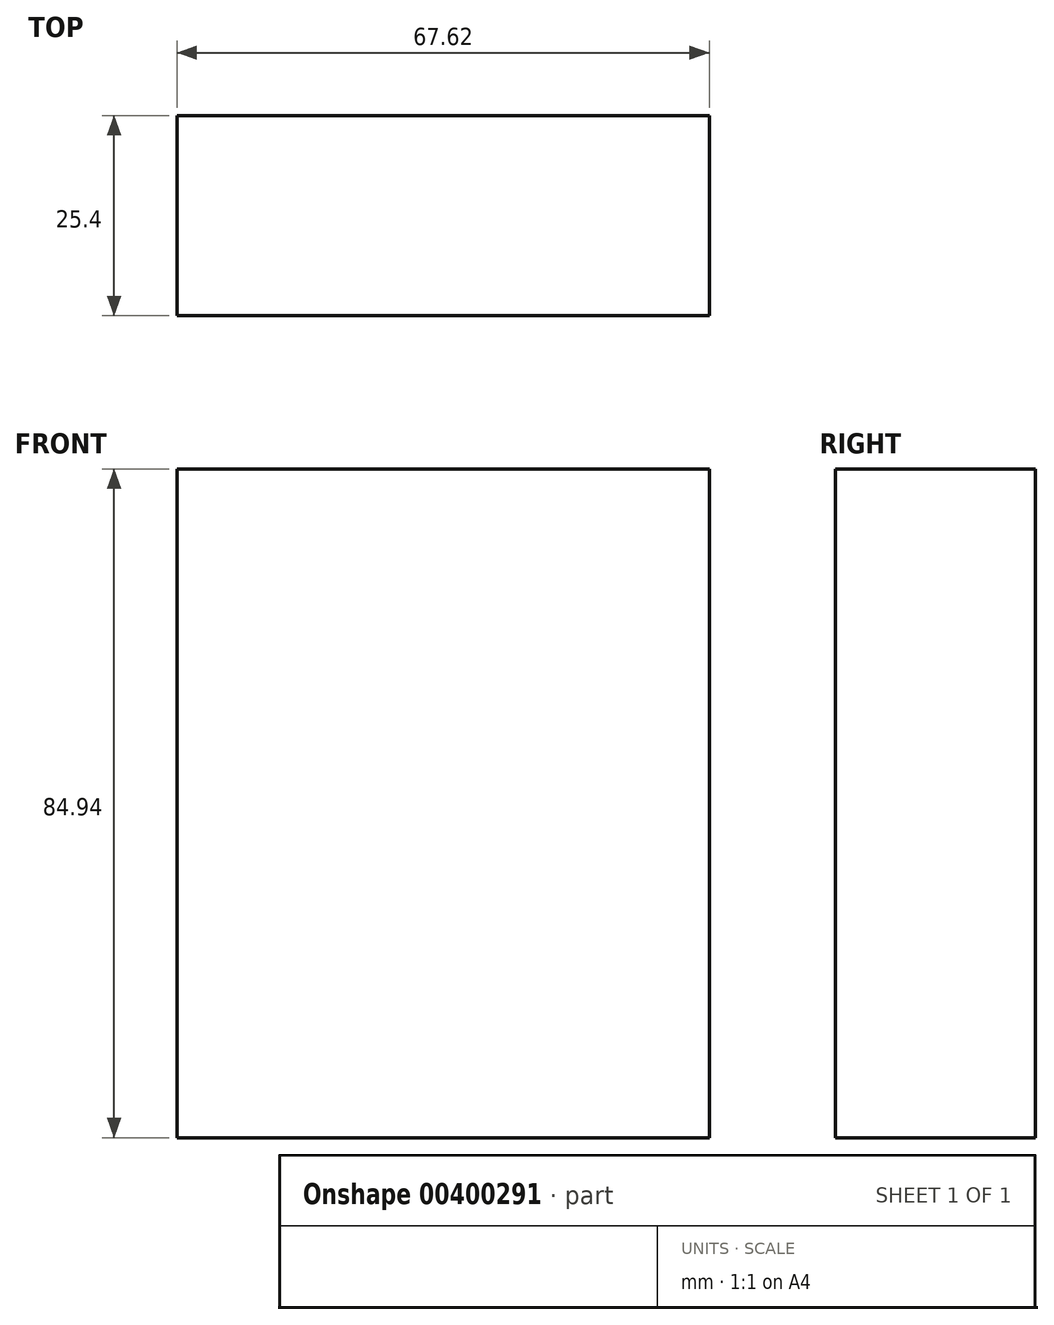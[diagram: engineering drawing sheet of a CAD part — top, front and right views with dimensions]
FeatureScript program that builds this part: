
annotation { "Feature Type Name" : "Feature", "Feature Type Description" : "" }
export const myFeature = defineFeature(function(context is Context, id is Id, definition is map)
    precondition{}
    {
        {
            var Q0;
            Q0=qCreatedBy(makeId("Front.planeOp"),FACE);
            var sketch = newSketch(context, id + "F0", { "sketchPlane" : qUnion([Q0])});
            skLineSegment(sketch, "E0.bottom", {"start": v(-198.99, 59.78) * mm, "end": v(-131.37, 59.78) * mm});
            skLineSegment(sketch, "E0.top", {"start": v(-198.99, -25.16) * mm, "end": v(-131.37, -25.16) * mm});
            skLineSegment(sketch, "E0.left", {"start": v(-198.99, 59.78) * mm, "end": v(-198.99, -25.16) * mm});
            skLineSegment(sketch, "E0.right", {"start": v(-131.37, 59.78) * mm, "end": v(-131.37, -25.16) * mm});
            skSolve(sketch);
        }
        {
            var Q0;
            Q0 = qSketchRegion(id + "F0", true);
            extrude(context, id + "F1", {"entities" : qUnion([Q0]), "depth" : 25.4 * mm});
        }
    });
